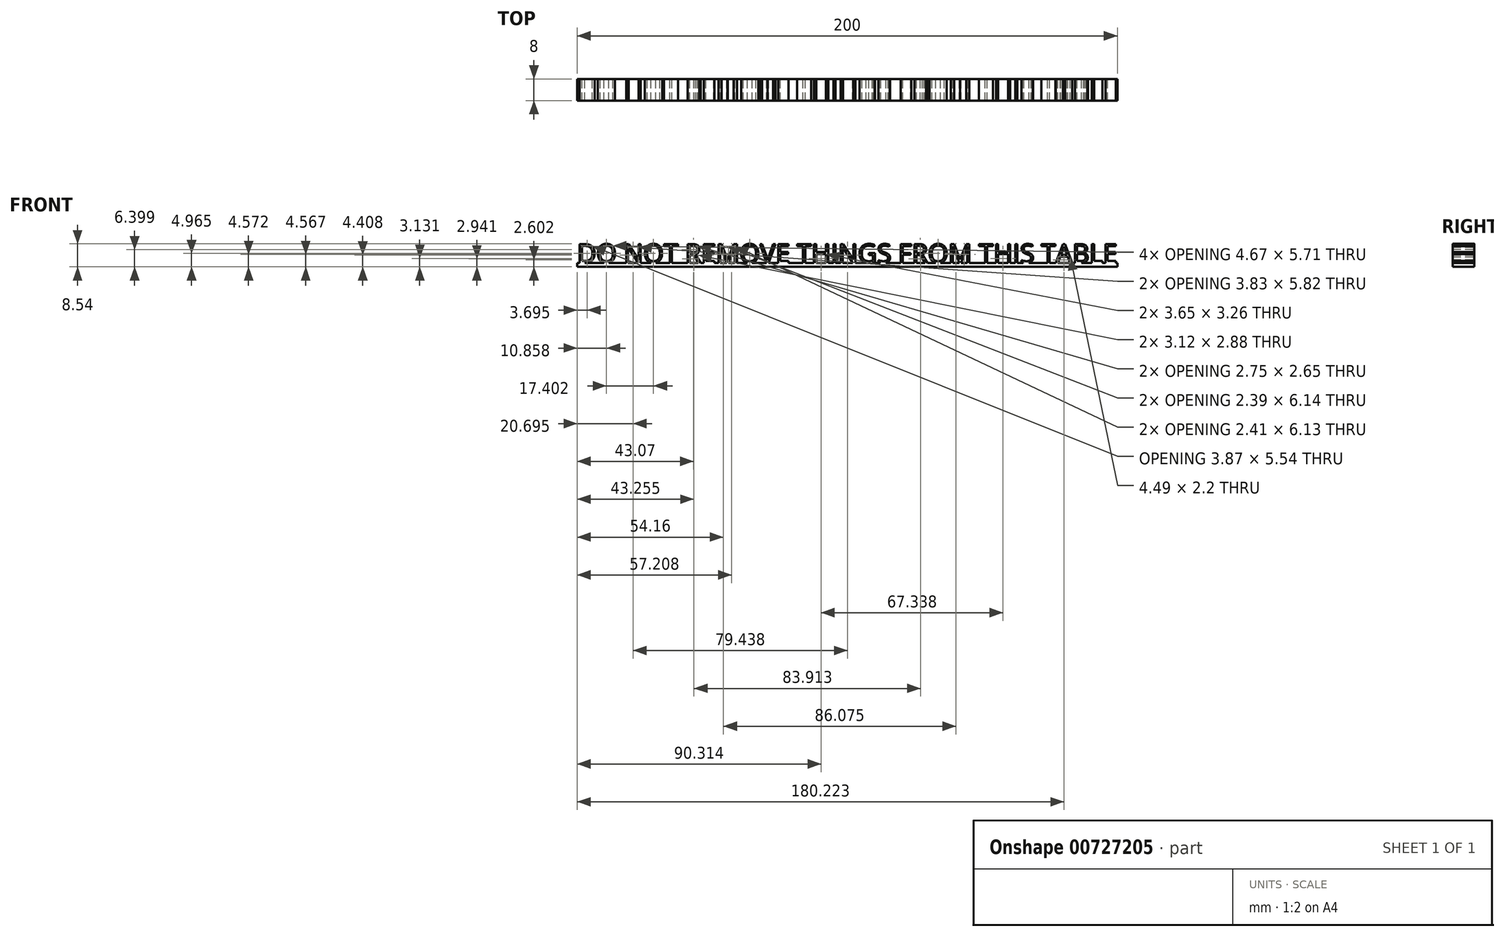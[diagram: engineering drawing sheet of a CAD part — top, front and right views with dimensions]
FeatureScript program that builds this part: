
annotation { "Feature Type Name" : "Feature", "Feature Type Description" : "" }
export const myFeature = defineFeature(function(context is Context, id is Id, definition is map)
    precondition{}
    {
        {
            var Q0;
            Q0=qCreatedBy(makeId("Front.planeOp"),FACE);
            var sketch = newSketch(context, id + "F0", { "sketchPlane" : qUnion([Q0])});
            skText(sketch, "E0", { "text": "DO NOT REMOVE THINGS FROM THIS TABLE", "fontName": "OpenSans-Regular.ttf"});
            skLineSegment(sketch, "E1.bottom", {"start": v(100, 1.5) * mm, "end": v(-100, 1.5) * mm});
            skLineSegment(sketch, "E1.top", {"start": v(100, 0) * mm, "end": v(-100, 0) * mm});
            skLineSegment(sketch, "E1.left", {"start": v(100, 1.5) * mm, "end": v(100, 0) * mm});
            skLineSegment(sketch, "E1.right", {"start": v(-100, 1.5) * mm, "end": v(-100, 0) * mm});
            const initialGuessF0  = {"E0": [-0.1, 0.0015, 1, 0, 0.00699]};
            skSetInitialGuess(sketch, initialGuessF0);
            skSolve(sketch);
        }
        {
            var Q0;
            {var subQ6=sQuery(id+"F0.wireOp",EDGE,"E0.sketch_text.stroke-401");var subQ7=sQuery(id+"F0.wireOp",EDGE,"E0.sketch_text.stroke-326");var subQ8=sQuery(id+"F0.wireOp",EDGE,"E0.sketch_text.stroke-325");var subQ9=makeQuery(id+"F0.imprint","INTERSECT",VERTEX,{"derivedFrom":[subQ8,subQ7]});var subQ13=sQuery(id+"F0.wireOp",EDGE,"E0.sketch_text.stroke-357");var subQ16=makeQuery(id+"F0.imprint","IMPRINT",EDGE,{"disambiguationData":[TD([[subQ9,1.0]])],"derivedFrom":subQ8});var subQ18=sQuery(id+"F0.wireOp",EDGE,"E0.sketch_text.stroke-61");var subQ19=sQuery(id+"F0.wireOp",EDGE,"E0.sketch_text.stroke-46");var subQ26=sQuery(id+"F0.wireOp",EDGE,"E0.sketch_text.stroke-238");var subQ27=sQuery(id+"F0.wireOp",EDGE,"E0.sketch_text.stroke-214");var subQ29=sQuery(id+"F0.wireOp",EDGE,"E0.sketch_text.stroke-308");var subQ30=makeQuery(id+"F0.imprint","IMPRINT",EDGE,{"derivedFrom":subQ29});var subQ31=sQuery(id+"F0.wireOp",EDGE,"E0.sketch_text.stroke-215");var subQ32=makeQuery(id+"F0.imprint","INTERSECT",VERTEX,{"derivedFrom":[subQ27,subQ31]});var subQ33=makeQuery(id+"F0.imprint","IMPRINT",EDGE,{"disambiguationData":[TD([[subQ32,1.0]])],"derivedFrom":subQ27});var subQ38=makeQuery(id+"F0.imprint","IMPRINT",EDGE,{"derivedFrom":subQ18});var subQ43=sQuery(id+"F0.wireOp",EDGE,"E0.sketch_text.stroke-196");var subQ44=makeQuery(id+"F0.imprint","IMPRINT",EDGE,{"derivedFrom":subQ43});var subQ48=sQuery(id+"F0.wireOp",EDGE,"E0.sketch_text.stroke-268");var subQ49=sQuery(id+"F0.wireOp",EDGE,"E0.sketch_text.stroke-267");var subQ50=makeQuery(id+"F0.imprint","INTERSECT",VERTEX,{"derivedFrom":[subQ49,subQ48]});var subQ52=makeQuery(id+"F0.imprint","IMPRINT",EDGE,{"disambiguationData":[TD([[subQ50,1.0]])],"derivedFrom":subQ49});var subQ56=sQuery(id+"F0.wireOp",EDGE,"E0.sketch_text.stroke-87");var subQ57=sQuery(id+"F0.wireOp",EDGE,"E0.sketch_text.stroke-178");var subQ58=makeQuery(id+"F0.imprint","IMPRINT",EDGE,{"derivedFrom":subQ57});var subQ64=sQuery(id+"F0.wireOp",EDGE,"E0.sketch_text.stroke-349");var subQ65=makeQuery(id+"F0.imprint","IMPRINT",EDGE,{"derivedFrom":subQ64});var subQ72=sQuery(id+"F0.wireOp",EDGE,"E0.sketch_text.stroke-47");var subQ73=makeQuery(id+"F0.imprint","INTERSECT",VERTEX,{"derivedFrom":[subQ19,subQ72]});var subQ79=sQuery(id+"F0.wireOp",EDGE,"E0.sketch_text.stroke-16");var subQ80=sQuery(id+"F0.wireOp",EDGE,"E0.sketch_text.stroke-15");var subQ81=makeQuery(id+"F0.imprint","INTERSECT",VERTEX,{"derivedFrom":[subQ80,subQ79]});var subQ84=sQuery(id+"F0.wireOp",EDGE,"E0.sketch_text.stroke-30");var subQ85=makeQuery(id+"F0.imprint","IMPRINT",EDGE,{"derivedFrom":subQ84});var subQ86=sQuery(id+"F0.wireOp",EDGE,"E0.sketch_text.stroke-300");var subQ87=makeQuery(id+"F0.imprint","IMPRINT",EDGE,{"derivedFrom":subQ86});var subQ88=sQuery(id+"F0.wireOp",EDGE,"E0.sketch_text.stroke-119");var subQ89=sQuery(id+"F0.wireOp",EDGE,"E0.sketch_text.stroke-118");var subQ90=makeQuery(id+"F0.imprint","INTERSECT",VERTEX,{"derivedFrom":[subQ89,subQ88]});var subQ93=makeQuery(id+"F0.imprint","IMPRINT",EDGE,{"derivedFrom":subQ6});var subQ94=sQuery(id+"F0.wireOp",EDGE,"E0.sketch_text.stroke-2");var subQ95=makeQuery(id+"F0.imprint","IMPRINT",EDGE,{"derivedFrom":subQ94});var subQ96=makeQuery(id+"F0.imprint","IMPRINT",EDGE,{"disambiguationData":[TD([[subQ73,1.0]])],"derivedFrom":subQ19});var subQ105=makeQuery(id+"F0.imprint","IMPRINT",EDGE,{"disambiguationData":[TD([[subQ81,1.0]])],"derivedFrom":subQ80});var subQ111=makeQuery(id+"F0.imprint","IMPRINT",EDGE,{"derivedFrom":subQ56});var subQ112=sQuery(id+"F0.wireOp",EDGE,"E0.sketch_text.stroke-154");var subQ113=makeQuery(id+"F0.imprint","IMPRINT",EDGE,{"derivedFrom":subQ112});var subQ114=sQuery(id+"F0.wireOp",EDGE,"E0.sketch_text.stroke-248");var subQ122=makeQuery(id+"F0.imprint","IMPRINT",EDGE,{"derivedFrom":subQ26});var subQ129=makeQuery(id+"F0.imprint","IMPRINT",EDGE,{"disambiguationData":[TD([[subQ90,1.0]])],"derivedFrom":subQ89});var subQ131=sQuery(id+"F0.wireOp",EDGE,"E0.sketch_text.stroke-142");var subQ132=makeQuery(id+"F0.imprint","IMPRINT",EDGE,{"derivedFrom":subQ131});var subQ134=sQuery(id+"F0.wireOp",EDGE,"E0.sketch_text.stroke-395");var subQ137=sQuery(id+"F0.wireOp",EDGE,"E0.sketch_text.stroke-162");var subQ138=makeQuery(id+"F0.imprint","IMPRINT",EDGE,{"derivedFrom":subQ137});var subQ170=sQuery(id+"F0.wireOp",EDGE,"E0.sketch_text.stroke-69");var subQ177=sQuery(id+"F0.wireOp",EDGE,"E0.sketch_text.stroke-99");var subQ179=sQuery(id+"F0.wireOp",EDGE,"E0.sketch_text.stroke-282");var subQ184=sQuery(id+"F0.wireOp",EDGE,"E0.sketch_text.stroke-320");var subQ186=sQuery(id+"F0.wireOp",EDGE,"E0.sketch_text.stroke-174");var subQ191=sQuery(id+"F0.wireOp",EDGE,"E0.sketch_text.stroke-266");var subQ196=sQuery(id+"F0.wireOp",EDGE,"E0.sketch_text.stroke-117");var subQ199=sQuery(id+"F0.wireOp",EDGE,"E0.sketch_text.stroke-45");var subQ202=sQuery(id+"F0.wireOp",EDGE,"E0.sketch_text.stroke-14");var subQ205=sQuery(id+"F0.wireOp",EDGE,"E0.sketch_text.stroke-324");var subQ207=sQuery(id+"F0.wireOp",EDGE,"E0.sketch_text.stroke-213");Q0=qUnion([makeQuery(id+"F0.imprint","IMPRINT",FACE,{"disambiguationData":[TD([[subQ38,-1.0]])]}),makeQuery(id+"F0.imprint","IMPRINT",FACE,{"disambiguationData":[TD([[subQ111,-1.0]])]}),makeQuery(id+"F0.imprint","IMPRINT",FACE,{"disambiguationData":[TD([[makeQuery(id+"F0.imprint","IMPRINT",EDGE,{"derivedFrom":sQuery(id+"F0.wireOp",EDGE,"E0.sketch_text.stroke-133")}),-1.0]])]}),makeQuery(id+"F0.imprint","IMPRINT",FACE,{"disambiguationData":[TD([[subQ132,-1.0]])]}),makeQuery(id+"F0.imprint","IMPRINT",FACE,{"disambiguationData":[TD([[subQ113,-1.0]])]}),makeQuery(id+"F0.imprint","IMPRINT",FACE,{"disambiguationData":[TD([[makeQuery(id+"F0.imprint","IMPRINT",EDGE,{"derivedFrom":subQ186}),-1.0]])]}),makeQuery(id+"F0.imprint","IMPRINT",FACE,{"disambiguationData":[TD([[makeQuery(id+"F0.imprint","IMPRINT",EDGE,{"derivedFrom":sQuery(id+"F0.wireOp",EDGE,"E0.sketch_text.stroke-193")}),-1.0]])]}),makeQuery(id+"F0.imprint","IMPRINT",FACE,{"disambiguationData":[TD([[makeQuery(id+"F0.imprint","IMPRINT",EDGE,{"derivedFrom":subQ207}),-1.0]])]}),makeQuery(id+"F0.imprint","IMPRINT",FACE,{"disambiguationData":[TD([[subQ122,-1.0]])]}),makeQuery(id+"F0.imprint","IMPRINT",FACE,{"disambiguationData":[TD([[subQ87,-1.0]])]}),makeQuery(id+"F0.imprint","IMPRINT",FACE,{"disambiguationData":[TD([[makeQuery(id+"F0.imprint","IMPRINT",EDGE,{"derivedFrom":subQ184}),-1.0]])]}),makeQuery(id+"F0.imprint","IMPRINT",FACE,{"disambiguationData":[TD([[makeQuery(id+"F0.imprint","IMPRINT",EDGE,{"derivedFrom":subQ205}),-1.0]])]}),makeQuery(id+"F0.imprint","IMPRINT",FACE,{"disambiguationData":[TD([[subQ65,-1.0]])]}),makeQuery(id+"F0.imprint","IMPRINT",FACE,{"disambiguationData":[TD([[makeQuery(id+"F0.imprint","IMPRINT",EDGE,{"derivedFrom":subQ134}),-1.0]])]}),makeQuery(id+"F0.imprint","IMPRINT",FACE,{"disambiguationData":[TD([[subQ93,-1.0]])]}),makeQuery(id+"F0.imprint","IMPRINT",FACE,{"disambiguationData":[TD([[makeQuery(id+"F0.imprint","IMPRINT",EDGE,{"derivedFrom":sQuery(id+"F0.wireOp",EDGE,"E0.sketch_text.stroke-0")}),-1.0]])]}),makeQuery(id+"F0.imprint","IMPRINT",FACE,{"disambiguationData":[TD([[makeQuery(id+"F0.imprint","IMPRINT",EDGE,{"derivedFrom":subQ202}),-1.0]])]}),makeQuery(id+"F0.imprint","IMPRINT",FACE,{"disambiguationData":[TD([[subQ105,-1.0]])]}),makeQuery(id+"F0.imprint","IMPRINT",FACE,{"disambiguationData":[TD([[subQ85,-1.0]])]}),makeQuery(id+"F0.imprint","IMPRINT",FACE,{"disambiguationData":[TD([[makeQuery(id+"F0.imprint","IMPRINT",EDGE,{"derivedFrom":subQ199}),-1.0]])]}),makeQuery(id+"F0.imprint","IMPRINT",FACE,{"disambiguationData":[TD([[subQ96,-1.0]])]}),makeQuery(id+"F0.imprint","IMPRINT",FACE,{"disambiguationData":[TD([[makeQuery(id+"F0.imprint","IMPRINT",EDGE,{"derivedFrom":subQ196}),-1.0]])]}),makeQuery(id+"F0.imprint","IMPRINT",FACE,{"disambiguationData":[TD([[subQ129,-1.0]])]}),makeQuery(id+"F0.imprint","IMPRINT",FACE,{"disambiguationData":[TD([[subQ138,-1.0]])]}),makeQuery(id+"F0.imprint","IMPRINT",FACE,{"disambiguationData":[TD([[subQ58,-1.0]])]}),makeQuery(id+"F0.imprint","IMPRINT",FACE,{"disambiguationData":[TD([[subQ44,-1.0]])]}),makeQuery(id+"F0.imprint","IMPRINT",FACE,{"disambiguationData":[TD([[subQ33,-1.0]])]}),makeQuery(id+"F0.imprint","IMPRINT",FACE,{"disambiguationData":[TD([[makeQuery(id+"F0.imprint","IMPRINT",EDGE,{"derivedFrom":subQ191}),-1.0]])]}),makeQuery(id+"F0.imprint","IMPRINT",FACE,{"disambiguationData":[TD([[subQ52,-1.0]])]}),makeQuery(id+"F0.imprint","IMPRINT",FACE,{"disambiguationData":[TD([[subQ30,-1.0]])]}),makeQuery(id+"F0.imprint","IMPRINT",FACE,{"disambiguationData":[TD([[subQ16,-1.0]])]}),makeQuery(id+"F0.imprint","IMPRINT",FACE,{"disambiguationData":[TD([[makeQuery(id+"F0.imprint","IMPRINT",EDGE,{"derivedFrom":subQ170}),-1.0]])]}),makeQuery(id+"F0.imprint","IMPRINT",FACE,{"disambiguationData":[TD([[makeQuery(id+"F0.imprint","IMPRINT",EDGE,{"derivedFrom":subQ177}),-1.0]])]}),makeQuery(id+"F0.imprint","IMPRINT",FACE,{"disambiguationData":[TD([[makeQuery(id+"F0.imprint","IMPRINT",EDGE,{"derivedFrom":subQ114}),-1.0]])]}),makeQuery(id+"F0.imprint","IMPRINT",FACE,{"disambiguationData":[TD([[makeQuery(id+"F0.imprint","IMPRINT",EDGE,{"derivedFrom":subQ179}),-1.0]])]}),makeQuery(id+"F0.imprint","IMPRINT",FACE,{"disambiguationData":[TD([[makeQuery(id+"F0.imprint","IMPRINT",EDGE,{"derivedFrom":subQ13}),-1.0]])]}),makeQuery(id+"F0.imprint","IMPRINT",FACE,{"disambiguationData":[TD([[makeQuery(id+"F0.imprint","IMPRINT",EDGE,{"derivedFrom":sQuery(id+"F0.wireOp",EDGE,"E0.sketch_text.stroke-370")}),-1.0]])]}),makeQuery(id+"F0.imprint","IMPRINT",FACE,{"disambiguationData":[TD([[subQ95,1.0]])]})]);}
            extrude(context, id + "F1", {"entities" : qUnion([Q0]), "depth" : 8 * mm, "offsetDistance" : 25.4 * mm});
        }
    });
